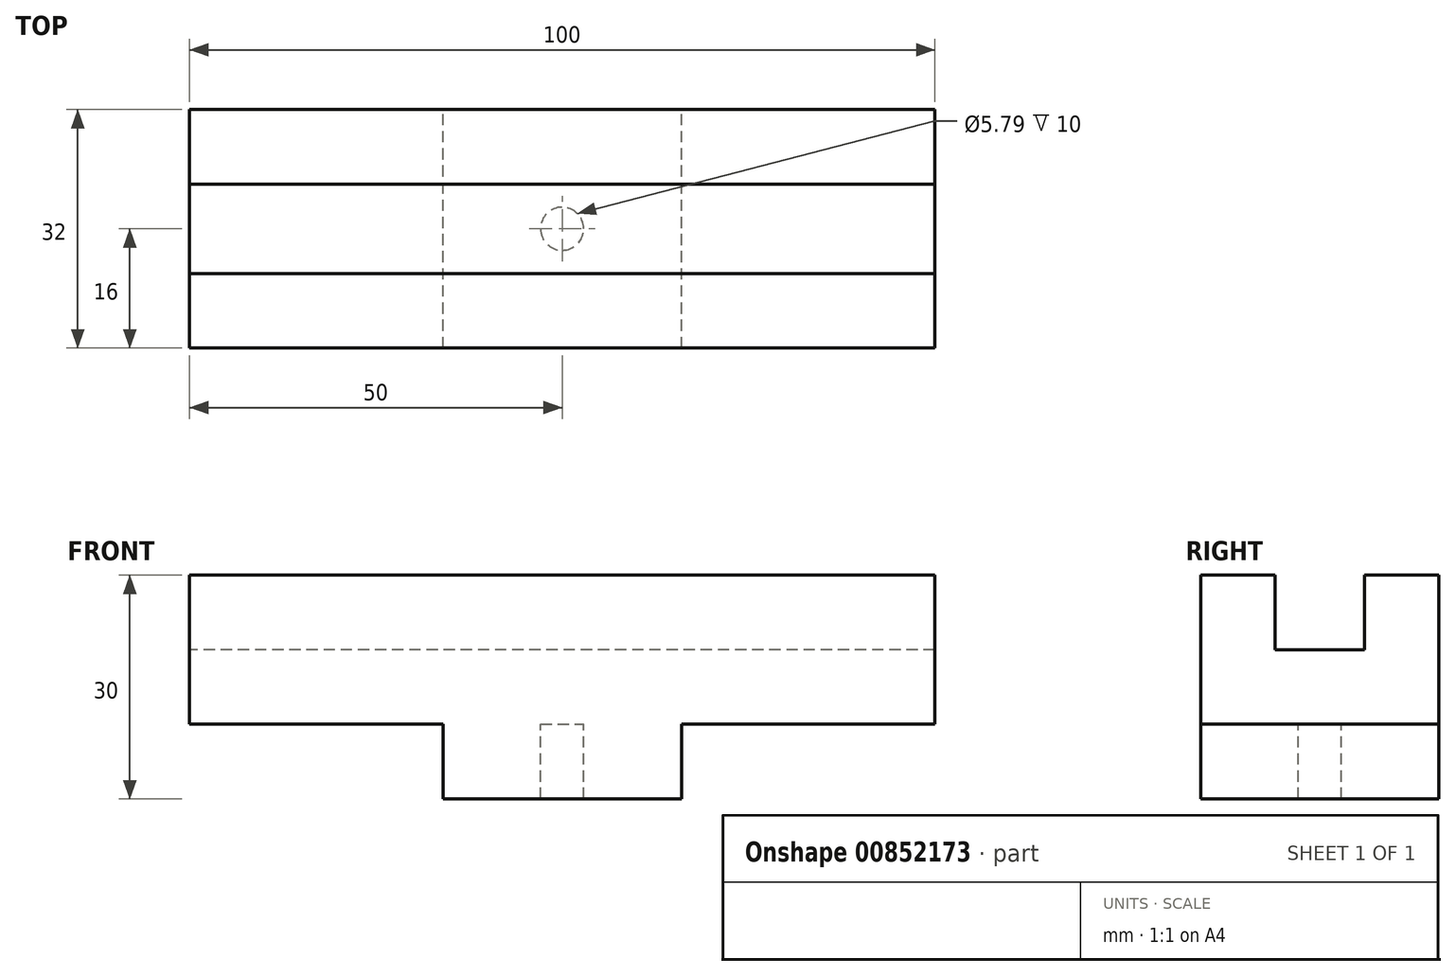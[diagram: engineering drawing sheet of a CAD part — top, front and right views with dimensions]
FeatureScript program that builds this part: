
annotation { "Feature Type Name" : "Feature", "Feature Type Description" : "" }
export const myFeature = defineFeature(function(context is Context, id is Id, definition is map)
    precondition{}
    {
        {
            var Q0;
            Q0=qCreatedBy(makeId("Right.planeOp"),FACE);
            var sketch = newSketch(context, id + "F0", { "sketchPlane" : qUnion([Q0])});
            skLineSegment(sketch, "E0", {"start": v(0, 10) * mm, "end": v(-6, 10) * mm});
            skLineSegment(sketch, "E1", {"start": v(-6, 10) * mm, "end": v(-6, 20) * mm});
            skLineSegment(sketch, "E2", {"start": v(-6, 20) * mm, "end": v(-16, 20) * mm});
            skLineSegment(sketch, "E3", {"start": v(-16, 20) * mm, "end": v(-16, 0) * mm});
            skLineSegment(sketch, "E4.MirrorCS", {"start": v(6, 10) * mm, "end": v(6, 20) * mm});
            skLineSegment(sketch, "E5.MirrorCS", {"start": v(16, 20) * mm, "end": v(16, 0) * mm});
            skLineSegment(sketch, "E6.MirrorCS", {"start": v(0, 10) * mm, "end": v(6, 10) * mm});
            skLineSegment(sketch, "E7.MirrorCS", {"start": v(6, 20) * mm, "end": v(16, 20) * mm});
            skLineSegment(sketch, "E8", {"start": v(-16, 0) * mm, "end": v(16, 0) * mm});
            skLineSegment(sketch, "E9", {"start": v(0, 10) * mm, "end": v(0, 0) * mm, "construction": true});
            skSolve(sketch);
        }
        {
            var Q0;
            Q0 = qSketchRegion(id + "F0", true);
            extrude(context, id + "F1", {"entities" : qUnion([Q0]), "endBound" : BoundingType.SYMMETRIC, "depth" : 100 * mm, "offsetDistance" : 25 * mm});
        }
        {
            var Q0;
            Q0=makeQuery(id+"F1.opExtrude","SWEPT_FACE",FACE,{"disambiguationData":[OSD([sQuery(id+"F0.wireOp",EDGE,"E8")])]});
            var sketch = newSketch(context, id + "F2", { "sketchPlane" : qUnion([Q0])});
            skLineSegment(sketch, "E10.bottom", {"start": v(-16, 16) * mm, "end": v(16, 16) * mm});
            skLineSegment(sketch, "E10.top", {"start": v(-16, -16) * mm, "end": v(16, -16) * mm});
            skLineSegment(sketch, "E10.left", {"start": v(-16, 16) * mm, "end": v(-16, -16) * mm});
            skLineSegment(sketch, "E10.right", {"start": v(16, 16) * mm, "end": v(16, -16) * mm});
            skCircle(sketch, "E11", {"center": v(0, 0) * mm, "radius": 2.9 * mm});
            skSolve(sketch);
        }
        {
            var Q0;
            Q0 = qSketchRegion(id + "F2", true);
            extrude(context, id + "F3", {"entities" : qUnion([Q0]), "operationType" : NewBodyOperationType.ADD, "depth" : 10 * mm, "offsetDistance" : 25 * mm});
        }
    });
